FCSTD DOCUMENT  (FreeCAD 0.16R6705 (Git))
Label: copri_L9R
License: All rights reserved
LicenseURL: http://it.wikipedia.org/wiki/<copyright redacted>
objects: Sketcher::SketchObject×4, PartDesign::Pocket×3, PartDesign::Revolution×1, Fem::FemMeshShapeNetgenObject×1, Fem::FemSetNodesObject×1, Fem::FemSolverObjectPython×1, Fem::ConstraintForce×1, Fem::FemAnalysisPython×1
note: 12 computed .brp shape members not serialized (recipe doc carries the construction recipe); baked Part::Feature solids carry a one-line shape summary decoded from their .brp

FEATURE [Sketcher::SketchObject] Sketch
  sketch-geometry (4):
    g0: ArcOfCircle CenterX=-26.0884 CenterY=1.3995 CenterZ=0 NormalX=0 NormalY=0 NormalZ=1 Radius=15.973 StartAngle=1.59467 EndAngle=3.22932
    g1: LineSegment StartX=-26.4697 StartY=17.368 StartZ=0 EndX=0 EndY=18 EndZ=0
    g2: LineSegment StartX=-42 StartY=0 StartZ=0 EndX=0 EndY=0 EndZ=0
    g3: LineSegment StartX=0 StartY=18 StartZ=0 EndX=0 EndY=0 EndZ=0
  constraints (10):
    c: Coincident(g1,g0)
    c: DistanceY(g-1,g1) = 18
    c: PointOnObject(g0,g-1)
    c: Tangent(g0,g1)
    c: PointOnObject(g1,g-2)
    c: DistanceX(g0,g-1) = 42
    c: Coincident(g2,g-1)
    c: Coincident(g2,g0)
    c: Coincident(g1,g3)
    c: Coincident(g-1,g3)
FEATURE [PartDesign::Revolution] Revolution
  Angle = 360
  Axis = (0,1,0)
  Base = (0,0,0)
  ReferenceAxis = -> Sketch [V_Axis]
  Sketch = -> Sketch
FEATURE [Sketcher::SketchObject] Sketch001
  Placement = pos=(0,0,0) rot=(1,0,0;1.5708rad)
  Support = -> Revolution [Face2]
  sketch-geometry (4):
    g0: LineSegment StartX=-15 StartY=30 StartZ=0 EndX=15 EndY=30 EndZ=0
    g1: LineSegment StartX=15 StartY=30 StartZ=0 EndX=15 EndY=-30 EndZ=0
    g2: LineSegment StartX=15 StartY=-30 StartZ=0 EndX=-15 EndY=-30 EndZ=0
    g3: LineSegment StartX=-15 StartY=-30 StartZ=0 EndX=-15 EndY=30 EndZ=0
  constraints (12):
    c: Coincident(g0,g1)
    c: Coincident(g1,g2)
    c: Coincident(g2,g3)
    c: Coincident(g3,g0)
    c: Horizontal(g0)
    c: Horizontal(g2)
    c: Vertical(g1)
    c: Vertical(g3)
    c: DistanceY(g3,g3) = 60
    c: DistanceX(g2,g2) = 30
    c: Symmetric(g0,g0,g-2)
    c: Symmetric(g0,g1,g-1)
FEATURE [PartDesign::Pocket] Pocket
  Length = 15
  Sketch = -> Sketch001
  Type = 0
FEATURE [Sketcher::SketchObject] Sketch002
  Placement = pos=(0,0,30) rot=(1,0,0;3.14159rad)
  Support = -> Pocket [Face4]
  sketch-geometry (4):
    g0: LineSegment StartX=5.20911 StartY=0.747133 StartZ=0 EndX=13.0378 EndY=0.747133 EndZ=0
    g1: LineSegment StartX=13.0378 StartY=0.747133 StartZ=0 EndX=13.0378 EndY=-2.16571 EndZ=0
    g2: LineSegment StartX=13.0378 StartY=-2.16571 StartZ=0 EndX=5.20911 EndY=-2.16571 EndZ=0
    g3: LineSegment StartX=5.20911 StartY=-2.16571 StartZ=0 EndX=5.20911 EndY=0.747133 EndZ=0
  constraints (8):
    c: Coincident(g0,g1)
    c: Coincident(g1,g2)
    c: Coincident(g2,g3)
    c: Coincident(g3,g0)
    c: Horizontal(g0)
    c: Horizontal(g2)
    c: Vertical(g1)
    c: Vertical(g3)
FEATURE [PartDesign::Pocket] Pocket001
  Length = 0
  Sketch = -> Sketch002
  Type = 1
FEATURE [Sketcher::SketchObject] Sketch003
  Placement = pos=(0,0,-30) rot=(0,0,1;0rad)
  Support = -> Pocket001 [Face9]
  sketch-geometry (4):
    g0: LineSegment StartX=5.57323 StartY=1.89277 StartZ=0 EndX=12.7647 EndY=1.89277 EndZ=0
    g1: LineSegment StartX=12.7647 StartY=1.89277 StartZ=0 EndX=12.7647 EndY=-0.656106 EndZ=0
    g2: LineSegment StartX=12.7647 StartY=-0.656106 StartZ=0 EndX=5.57323 EndY=-0.656106 EndZ=0
    g3: LineSegment StartX=5.57323 StartY=-0.656106 StartZ=0 EndX=5.57323 EndY=1.89277 EndZ=0
  constraints (8):
    c: Coincident(g0,g1)
    c: Coincident(g1,g2)
    c: Coincident(g2,g3)
    c: Coincident(g3,g0)
    c: Horizontal(g0)
    c: Horizontal(g2)
    c: Vertical(g1)
    c: Vertical(g3)
FEATURE [PartDesign::Pocket] Pocket002
  Length = 5
  Sketch = -> Sketch003
  Type = 1
FEATURE [Fem::FemMeshShapeNetgenObject] Pocket002_Mesh
  Fineness = 2
  GrowthRate = 0.3
  MaxSize = 1000
  NbSegsPerEdge = 1
  NbSegsPerRadius = 2
  Optimize = true
  SecondOrder = true
  Shape = -> Pocket002
FEATURE [Fem::FemSetNodesObject] NodesSet
  FemMesh = -> Pocket002_Mesh
FEATURE [Fem::FemSolverObjectPython] CalculiX  # FEM object (typed FeaturePython)
  AnalysisType = 0
  EigenmodeHighLimit = 1000000
  EigenmodeLowLimit = 0
  NumberOfEigenmodes = 10
  SolverType = FemSolverCalculix
FEATURE [Fem::ConstraintForce] FemConstraintForce
  DirectionVector = (0.745443,0.66657,0)
  Force = 1
  NormalDirection = (0.745443,0.66657,0)
  Points = (16) [(-26.4697,17.368,0),(13.2348,17.368,22.9234),(13.2348,17.368,-22.9234),(-26.4697,17.368,-6.4832e-15),(-34.6912,14.8579,0),(17.3456,14.8579,30.0435),+10 more]
  References = -> [Pocket002]
  Scale = 6
FEATURE [Fem::FemAnalysisPython] MechanicalAnalysis  # FEM object (typed FeaturePython)
  Member = -> [CalculiX,Pocket002_Mesh,FemConstraintForce]
